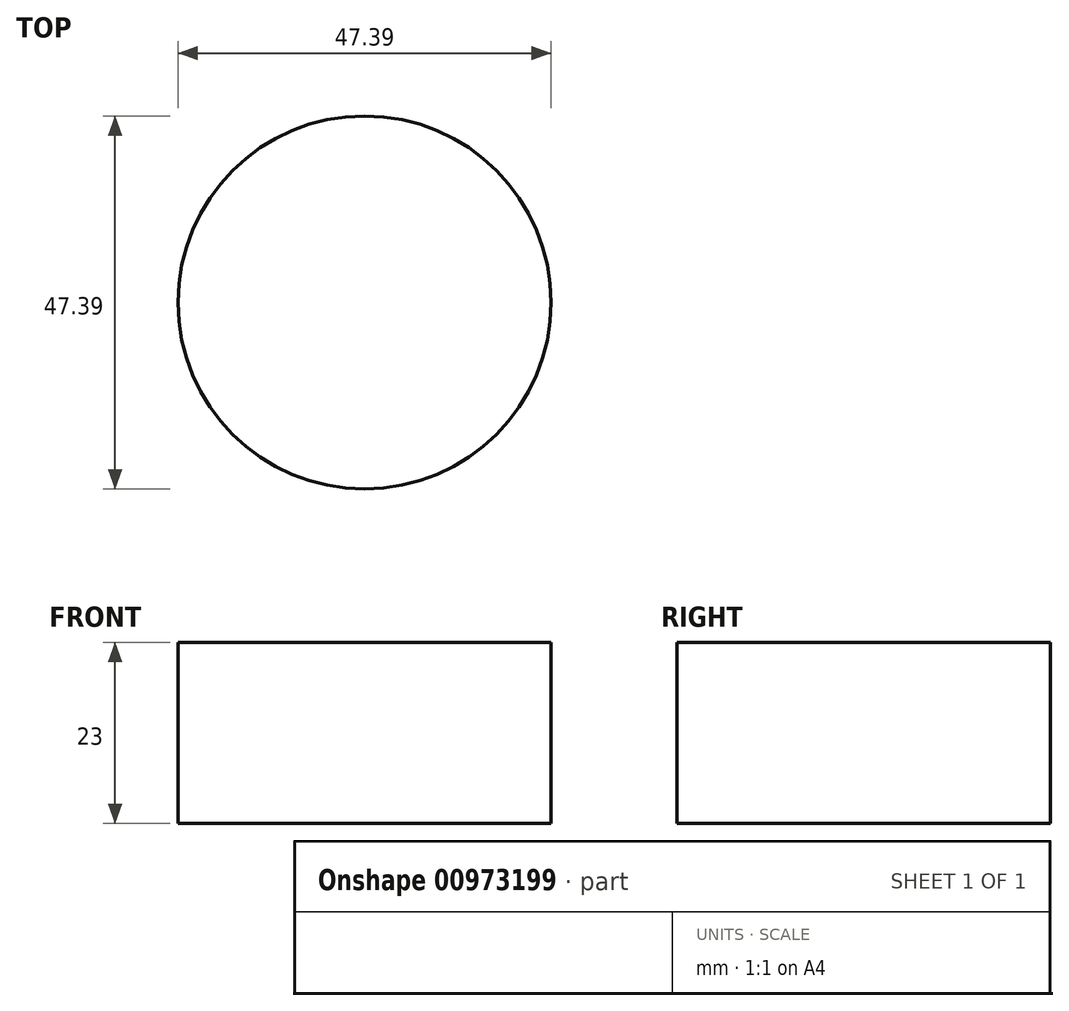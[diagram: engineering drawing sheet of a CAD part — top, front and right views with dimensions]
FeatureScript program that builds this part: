
annotation { "Feature Type Name" : "Feature", "Feature Type Description" : "" }
export const myFeature = defineFeature(function(context is Context, id is Id, definition is map)
    precondition{}
    {
        {
            var Q0;
            Q0=qCreatedBy(makeId("Top.planeOp"),FACE);
            var sketch = newSketch(context, id + "F0", { "sketchPlane" : qUnion([Q0])});
            skCircle(sketch, "E0", {"center": v(-7.3, 42.33) * mm, "radius": 23.7 * mm});
            skSolve(sketch);
        }
        {
            var Q0;
            Q0=makeQuery(id+"F0.imprint","IMPRINT",FACE,{"disambiguationData":[TD([[makeQuery(id+"F0.imprint","IMPRINT",EDGE,{"derivedFrom":sQuery(id+"F0.wireOp",EDGE,"E0")}),1.0]])]});
            extrude(context, id + "F1", {"entities" : qUnion([Q0]), "depth" : 23 * mm, "offsetDistance" : 25.4 * mm});
        }
    });
